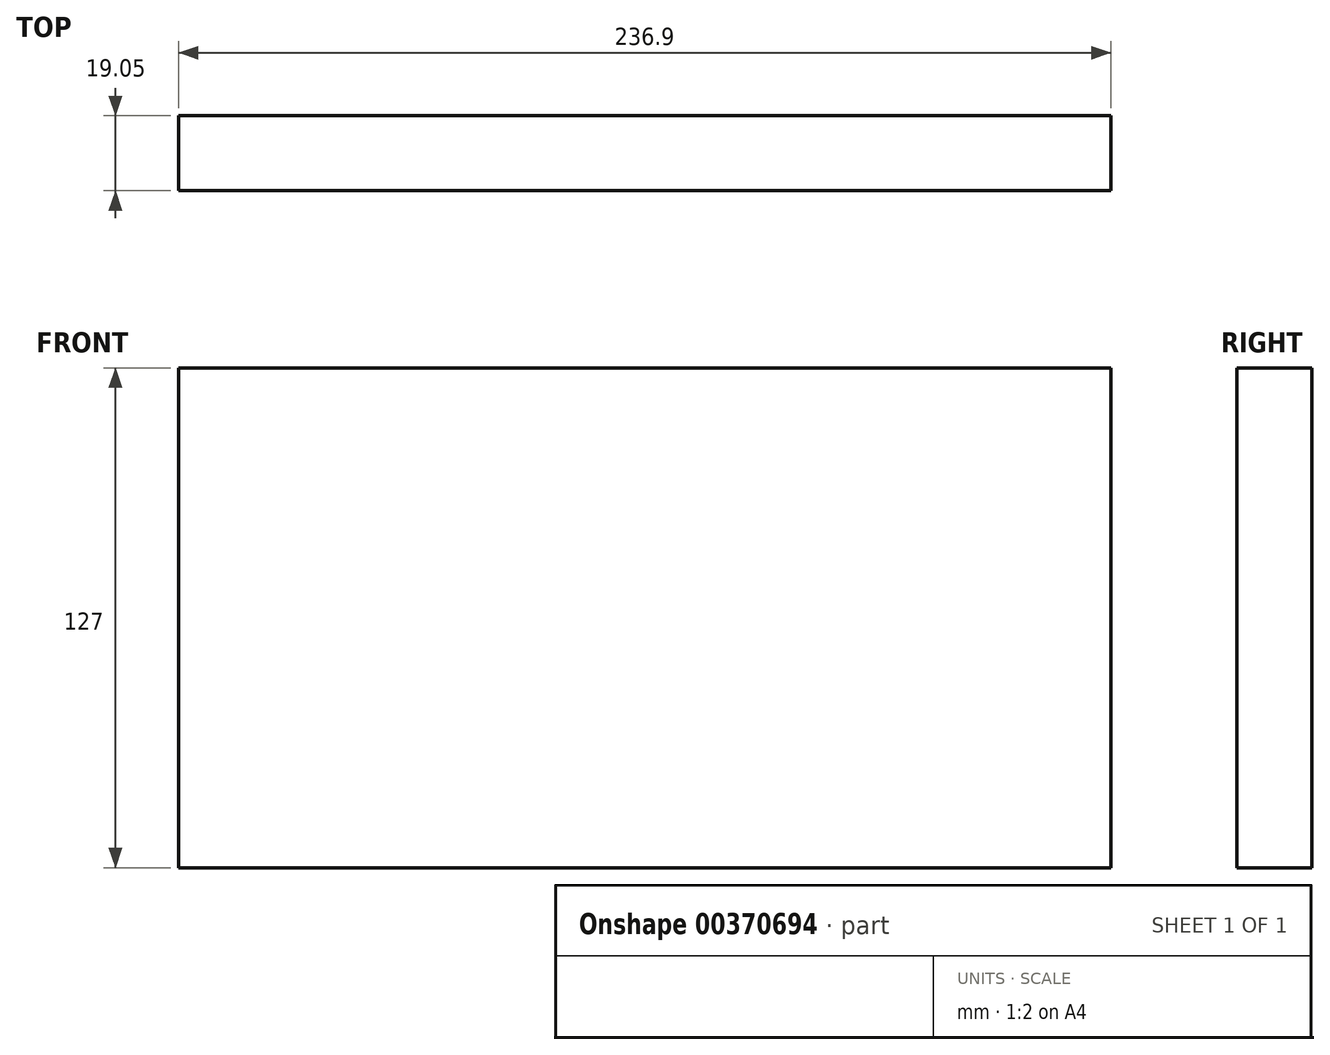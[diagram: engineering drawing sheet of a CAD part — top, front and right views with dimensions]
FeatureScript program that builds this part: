
annotation { "Feature Type Name" : "Feature", "Feature Type Description" : "" }
export const myFeature = defineFeature(function(context is Context, id is Id, definition is map)
    precondition{}
    {
        {
            var Q0;
            Q0=qCreatedBy(makeId("Front.planeOp"),FACE);
            var sketch = newSketch(context, id + "F0", { "sketchPlane" : qUnion([Q0])});
            skLineSegment(sketch, "E0.bottom", {"start": v(0, 0) * mm, "end": v(0, 0) * mm});
            skLineSegment(sketch, "E0.top", {"start": v(0, 0) * mm, "end": v(0, 0) * mm});
            skLineSegment(sketch, "E0.left", {"start": v(0, 0) * mm, "end": v(0, 0) * mm});
            skLineSegment(sketch, "E0.right", {"start": v(0, 0) * mm, "end": v(0, 0) * mm});
            skPoint(sketch, "E0.middle", {"position": v(0, 0) * mm});
            skLineSegment(sketch, "E1.bottom", {"start": v(178.03, 152.45) * mm, "end": v(-58.87, 152.45) * mm});
            skLineSegment(sketch, "E1.top", {"start": v(178.03, 25.45) * mm, "end": v(-58.87, 25.45) * mm});
            skLineSegment(sketch, "E1.left", {"start": v(178.03, 152.45) * mm, "end": v(178.03, 25.45) * mm});
            skLineSegment(sketch, "E1.right", {"start": v(-58.87, 152.45) * mm, "end": v(-58.87, 25.45) * mm});
            skPoint(sketch, "E1.middle", {"position": v(59.58, 88.95) * mm});
            skSolve(sketch);
        }
        {
            var Q0;
            Q0=makeQuery(id+"F0.imprint","IMPRINT",FACE,{"disambiguationData":[TD([[makeQuery(id+"F0.imprint","IMPRINT",EDGE,{"derivedFrom":sQuery(id+"F0.wireOp",EDGE,"E1.bottom")}),1.0]])]});
            extrude(context, id + "F1", {"entities" : qUnion([Q0]), "depth" : 19.05 * mm});
        }
    });
